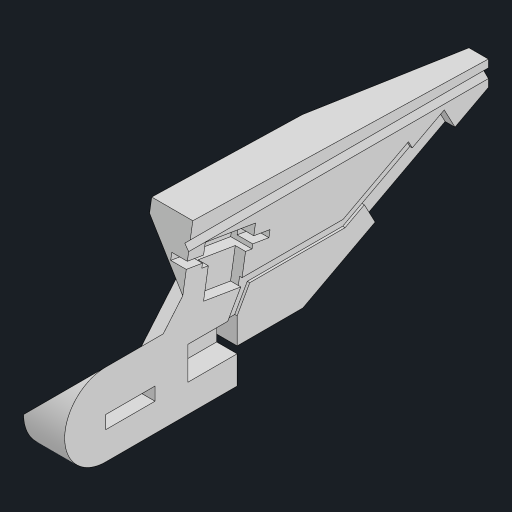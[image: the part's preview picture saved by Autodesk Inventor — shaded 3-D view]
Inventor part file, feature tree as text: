
AUTODESK INVENTOR PART (.ipt)
format: ipt  version: 2023 (Build 270158000, 158)  size: 463,872 bytes
history: native  units: mm
features: extrude x16, other x11, sketch x11, projected_geometry x11
ambient origin geometry x8: Origin, YZ Plane, XZ Plane, XY Plane, X Axis, Y Axis, Z Axis, Center Point
bodies: Body1 (feature_tree)
feature tree (49):
  other  "ソリッド1"
  extrude  "押し出し1"  Depth=0.261799mm
  other  "作業平面1"
  other  "作業平面3"
  extrude  "押し出し5"  Depth=37.0mm
  extrude  "押し出し6"  Depth=25.0mm
  other  "おでこ"
  other  "作業平面4"
  extrude  "押し出し7"  Depth=22.68928mm
  other  "作業平面5"
  extrude  "押し出し8"  Depth=1.658063mm
  extrude  "押し出し9"  Depth=3.0mm
  other  "作業平面9"
  extrude  "押し出し16"  Depth=180.0mm
  other  "作業平面11"
  extrude  "押し出し11"  Depth=19.2mm
  extrude  "押し出し12"  Depth=5.0mm
  extrude  "押し出し13"  Depth=180.0mm
  extrude  "押し出し15"  Depth=15.0mm
  extrude  "貫通"  Depth=50.0mm TaperAngle=0.0deg
  other  "YZ平面"
  other  "XZ平面"
  extrude  "サーボ"  Depth=50.0mm
  extrude  "基板"  Depth=25.0mm TaperAngle=90.0deg
  extrude  "押し出し27"  Depth=13.962634mm
  other  "サーボ位置合わせ"
  extrude  "右半分"  Depth=11.34464mm
  sketch  "スケッチ1"
  sketch  "スケッチ5"
  sketch  "スケッチ6"
  sketch  "スケッチ8"
  sketch  "スケッチ9"
  sketch  "スケッチ10"
  projected_geometry  "投影ループ1"
  projected_geometry  "投影ループ2"
  sketch  "スケッチ14"
  sketch  "スケッチ16"
  projected_geometry  "投影ループ3"
  sketch  "スケッチ20"
  projected_geometry  "投影ループ7"
  sketch  "スケッチ26"
  projected_geometry  "投影ループ10"
  projected_geometry  "投影ループ12"
  sketch  "スケッチ29"
  projected_geometry  "投影ループ13"
  projected_geometry  "投影ループ14"
  projected_geometry  "投影ループ15"
  projected_geometry  "投影ループ16"
  projected_geometry  "投影ループ17"
